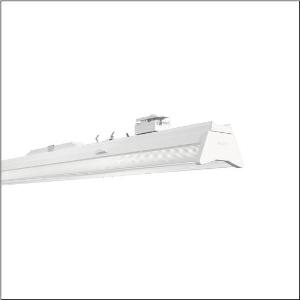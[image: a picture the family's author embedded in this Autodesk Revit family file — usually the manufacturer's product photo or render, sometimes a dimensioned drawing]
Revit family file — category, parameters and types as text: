
# Revit family: licross_r__21_performance_mo_52td16mn4a5g_2767
name_source: partatom
category: Lighting Fixtures
units: mm (PartAtom-declared; Revit-internal decimal feet)

## family parameters
Cut with Voids When Loaded = No
Host = Face
Light Source = No
Part Type = Normal
Room Calculation Point = No
Round Connector Dimension = Use Diameter
Shared = No

## types (1)
- --- (1 x LED, 10890 lm, 60.5 W, 4000K)
    Apparent Load = 61 VA
    CIE Flux Codes = 66 88 96 79 100
    Color Rendering = 80
    Color Temperature = 4000K
    Default Elevation = 1800 mm
    Description = Licross® 21 Performance MO, luminaire insert, of sheet steel, galvanised, coil coated, white, length: 1.500mm, width: 120mm, height: 123mm, LED rated luminous flux: 10.890lm, light colour: 840, control gear: ON/OFF Multilumen, with plug, 3-pole, with phase selection, mains connection: 220..240V, AC, 50/60Hz, rated input power: 61W, halogen-free wiring, primary light control with lens, of plastic, primary optical cover: cover, of PMMA, light emission: direct/indirect distribution, primary light characteristic: symmetric, protection rating (complete): IP54, insulation class (complete): insulation class I (protective earthing), certification: CE, ENEC, UKCA, protection symbol: D if used in an environment with non-conductive dust loads with corresponding accessories, impact resistance: IK06, permissible ambient temperature for indoor applications: -35..+45°C, corresponds to IFS (International Featured Standards) requirements for safety and quality in the food industry, reducing of maximum allowable ambient temperature of 5°C with ceiling mounting, LABS conformity tested according to VDMA 24364:2018-05, packaging unit: 1 piece
    Height = 114 mm
    Lamp = 1 x LED
    Lamp Light Flux = 10890 lm
    Lamp Power = 60.5 W
    Lamp count = 1
    Length = 1500 mm
    Luminous efficacy = 180 lm/W
    Manufacturer = Siteco
    ModVariant = No
    Model = 52TD16MN4A5G
    Mounting Place = Ceiling
    Mounting Type = Pendant
    Number of Poles = 1
    OnlyDefault = Yes
    Power Factor = 1
    Product Name = Licross® 21 Performance MO
    Product group = luminaire insert
    ProductGroupID = 901
    Protection Class = Protection class I
    Protection Degree = IP 54
    RLX_Detail_Level = 1
    RLX_Emergency_Light_Flux = 0 lm
    RLX_Emergency_Type = 0
    RLX_Emergency_Type_DB = No
    RlxData = <blob elided: 31849 chars, md5=c8d213a3>
    Socket = socket
    Standby Power = 0 W
    System Light Flux = 10890 lm
    System Power = 61 W
    Type Comments = factory setting: luminous flux: 100 % | (A | C | E) | 140 mA
    Type Image = l_1256138.jpg
    URL = http://relux.com
    VarID = @adj_057509
    Voltage = 0 V
    Weight = 0.00 kg
    Width = 120 mm

## geometry (parser evidence)
native form markers: Blend x4, Sweep x12
no freeform markers — native parametric forms only
